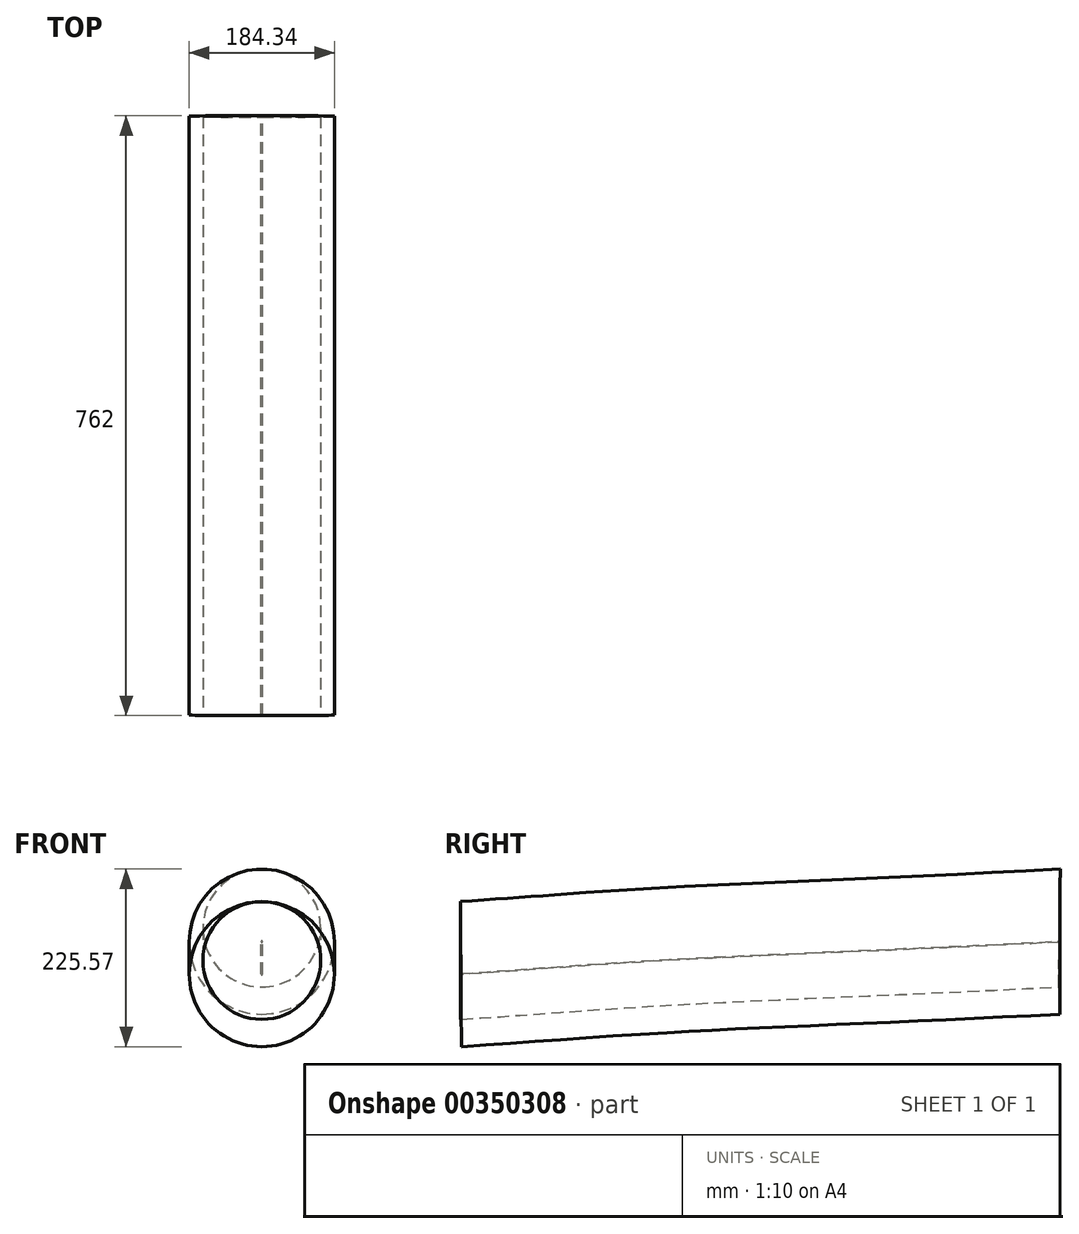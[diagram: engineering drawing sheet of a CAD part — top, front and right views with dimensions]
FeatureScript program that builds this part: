
annotation { "Feature Type Name" : "Feature", "Feature Type Description" : "" }
export const myFeature = defineFeature(function(context is Context, id is Id, definition is map)
    precondition{}
    {
        {
            var Q0;
            Q0=qCreatedBy(makeId("Front.planeOp"),FACE);
            var sketch = newSketch(context, id + "F0", { "sketchPlane" : qUnion([Q0])});
            skCircle(sketch, "E0", {"center": v(0, 0) * mm, "radius": 74.84 * mm});
            skSolve(sketch);
        }
        {
            var Q0;
            Q0=qCreatedBy(makeId("Front.planeOp"),FACE);
            cPlane(context, id + "F1", {"entities" : qUnion([Q0]), "cplaneType" : CPlaneType.OFFSET, "offset" : 254 * mm, "oppositeDirection" : true, "width" : 152.4 * mm, "height" : 152.4 * mm});
        }
        {
            var Q0;
            Q0=qCreatedBy(id+"F1.planeOp",FACE);
            var sketch = newSketch(context, id + "F2", { "sketchPlane" : qUnion([Q0])});
            skCircle(sketch, "E1", {"center": v(0, 0) * mm, "radius": 0.7 * mm});
            skCircle(sketch, "E2", {"center": v(0, 0) * mm, "radius": 92.17 * mm});
            skSolve(sketch);
        }
        {
            var Q0;
            Q0=qCreatedBy(makeId("Front.planeOp"),FACE);
            cPlane(context, id + "F3", {"entities" : qUnion([Q0]), "cplaneType" : CPlaneType.OFFSET, "offset" : 762 * mm, "oppositeDirection" : true, "width" : 152.4 * mm, "height" : 152.4 * mm});
        }
        {
            var Q0;
            Q0=qCreatedBy(id+"F3.planeOp",FACE);
            var sketch = newSketch(context, id + "F4", { "sketchPlane" : qUnion([Q0])});
            skCircle(sketch, "E3", {"center": v(0, 0) * mm, "radius": 116.07 * mm});
            skSolve(sketch);
        }
        {
            var Q0;
            Q0=qCreatedBy(makeId("Right.planeOp"),FACE);
            var sketch = newSketch(context, id + "F5", { "sketchPlane" : qUnion([Q0])});
            skLineSegment(sketch, "E4.0", {"start": v(254, -92.17) * mm, "end": v(254, 92.17) * mm, "construction": true});
            skLineSegment(sketch, "E5.0", {"start": v(762, -116.07) * mm, "end": v(762, 116.07) * mm, "construction": true});
            skLineSegment(sketch, "E6.0", {"start": v(0, -74.84) * mm, "end": v(0, 74.84) * mm, "construction": true});
            skSolve(sketch);
        }
        {
            var Q0;
            Q0=qCreatedBy(makeId("Right.planeOp"),FACE);
            var sketch = newSketch(context, id + "F6", { "sketchPlane" : qUnion([Q0])});
            skFitSpline(sketch, "E7", {"points": [v(0, 74.84) * mm, v(254, 92.17) * mm, v(762, 116.07) * mm], "startDerivative": vector(563.15, 36.54) * mm, "endDerivative": vector(937.75, 50.13) * mm});
            skSolve(sketch);
        }
        {
            var Q0;
            Q0=makeQuery(id+"F0.imprint","IMPRINT",FACE,{"disambiguationData":[TD([[makeQuery(id+"F0.imprint","IMPRINT",EDGE,{"derivedFrom":sQuery(id+"F0.wireOp",EDGE,"E0")}),1.0]])]});
            var Q1;
            Q1=makeQuery(id+"F2.imprint","IMPRINT",FACE,{"disambiguationData":[TD([[makeQuery(id+"F2.imprint","IMPRINT",EDGE,{"derivedFrom":sQuery(id+"F2.wireOp",EDGE,"E1")}),-1.0]])]});
            var Q2;
            Q2=makeQuery(id+"F4.imprint","IMPRINT",FACE,{"disambiguationData":[TD([[makeQuery(id+"F4.imprint","IMPRINT",EDGE,{"derivedFrom":sQuery(id+"F4.wireOp",EDGE,"E3")}),1.0]])]});
            var Q3;
            Q3=sQuery(id+"F6.wireOp",EDGE,"E7");
            sweep(context, id + "F7", {"profiles" : qUnion([Q0, Q1, Q2]), "path" : qUnion([Q3])});
        }
        {
            var Q0;
            Q0=makeQuery(id+"F7.opSweep","SWEPT_BODY",BODY,{"disambiguationData":[OSD([sQuery(id+"F4.wireOp",EDGE,"E3"),sQuery(id+"F6.wireOp",EDGE,"E7")])]});
            deleteBodies(context, id + "F8", {"entities" : qUnion([Q0])});
        }
    });
